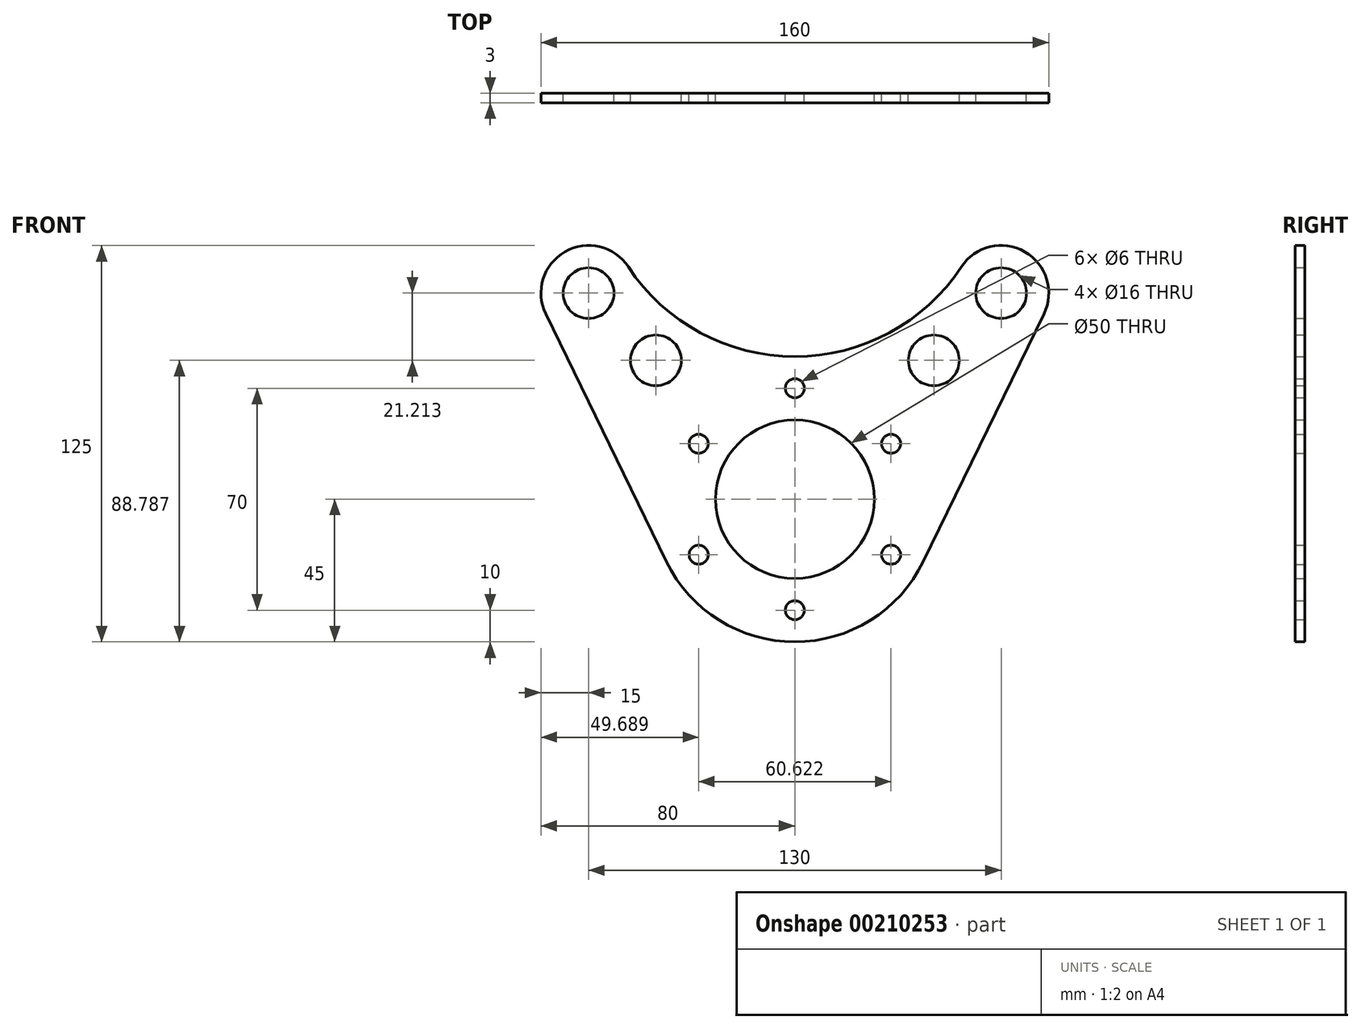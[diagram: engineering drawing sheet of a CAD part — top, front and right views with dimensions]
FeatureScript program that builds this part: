
annotation { "Feature Type Name" : "Feature", "Feature Type Description" : "" }
export const myFeature = defineFeature(function(context is Context, id is Id, definition is map)
    precondition{}
    {
        {
            var Q0;
            Q0=qCreatedBy(makeId("Front.planeOp"),FACE);
            var sketch = newSketch(context, id + "F0", { "sketchPlane" : qUnion([Q0])});
            skCircle(sketch, "E0", {"center": v(0, 0) * mm, "radius": 45 * mm});
            skCircle(sketch, "E1", {"center": v(-65, 65) * mm, "radius": 15 * mm});
            skCircle(sketch, "E2", {"center": v(65, 65) * mm, "radius": 15 * mm});
            skCircle(sketch, "E3", {"center": v(-65, 65) * mm, "radius": 8 * mm});
            skCircle(sketch, "E4", {"center": v(65, 65) * mm, "radius": 8 * mm});
            skLineSegment(sketch, "E5", {"start": v(-78.49, 58.44) * mm, "end": v(-40.46, -19.7) * mm});
            skLineSegment(sketch, "E6", {"start": v(78.49, 58.44) * mm, "end": v(40.46, -19.7) * mm});
            skArc(sketch, "E7", {"start": v(-52.48, 73.26) * mm, "mid": v(-29.8, 52.51) * mm, "end": v(0, 45) * mm});
            skArc(sketch, "E8", {"start": v(0, 45) * mm, "mid": v(29.8, 52.51) * mm, "end": v(52.48, 73.26) * mm});
            skCircle(sketch, "E9", {"center": v(0, 0) * mm, "radius": 25 * mm});
            skCircle(sketch, "E10", {"center": v(-43.79, 43.79) * mm, "radius": 8 * mm});
            skCircle(sketch, "E11", {"center": v(43.79, 43.79) * mm, "radius": 8 * mm});
            skCircle(sketch, "E12", {"center": v(0, 35) * mm, "radius": 3 * mm});
            skCircle(sketch, "E13.1.0", {"center": v(-30.31, 17.5) * mm, "radius": 3 * mm});
            skCircle(sketch, "E13.2.0", {"center": v(-30.31, -17.5) * mm, "radius": 3 * mm});
            skCircle(sketch, "E13.3.0", {"center": v(0, -35) * mm, "radius": 3 * mm});
            skCircle(sketch, "E13.4.0", {"center": v(30.31, -17.5) * mm, "radius": 3 * mm});
            skCircle(sketch, "E13.5.0", {"center": v(30.31, 17.5) * mm, "radius": 3 * mm});
            skSolve(sketch);
        }
        {
            var Q0;
            {var subQ1=sQuery(id+"F0.wireOp",EDGE,"E5");Q0=makeQuery(id+"F0.imprint","IMPRINT",FACE,{"disambiguationData":[TD([[makeQuery(id+"F0.imprint","IMPRINT",EDGE,{"derivedFrom":subQ1}),1.0]])]});}
            var Q1;
            Q1=makeQuery(id+"F0.imprint","IMPRINT",FACE,{"disambiguationData":[TD([[makeQuery(id+"F0.imprint","IMPRINT",EDGE,{"derivedFrom":sQuery(id+"F0.wireOp",EDGE,"E3")}),-1.0]])]});
            var Q2;
            Q2=makeQuery(id+"F0.imprint","IMPRINT",FACE,{"disambiguationData":[TD([[makeQuery(id+"F0.imprint","IMPRINT",EDGE,{"derivedFrom":sQuery(id+"F0.wireOp",EDGE,"E9")}),-1.0]])]});
            var Q3;
            {var subQ1=sQuery(id+"F0.wireOp",EDGE,"E6");Q3=makeQuery(id+"F0.imprint","IMPRINT",FACE,{"disambiguationData":[TD([[makeQuery(id+"F0.imprint","IMPRINT",EDGE,{"derivedFrom":subQ1}),-1.0]])]});}
            var Q4;
            Q4=makeQuery(id+"F0.imprint","IMPRINT",FACE,{"disambiguationData":[TD([[makeQuery(id+"F0.imprint","IMPRINT",EDGE,{"derivedFrom":sQuery(id+"F0.wireOp",EDGE,"E4")}),-1.0]])]});
            extrude(context, id + "F1", {"entities" : qUnion([Q0, Q1, Q2, Q3, Q4]), "endBound" : BoundingType.SYMMETRIC, "depth" : 3 * mm});
        }
    });
